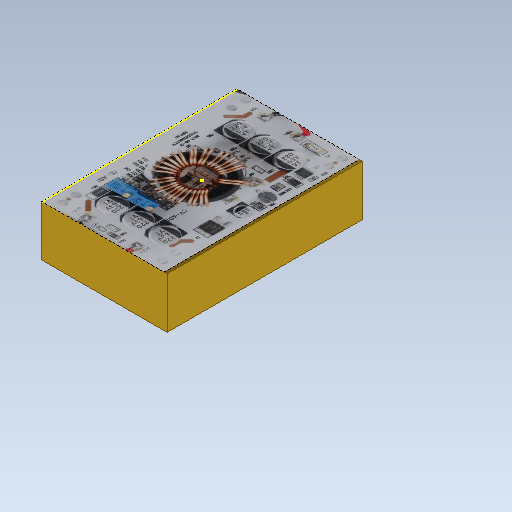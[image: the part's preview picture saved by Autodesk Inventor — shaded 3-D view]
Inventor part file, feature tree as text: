
AUTODESK INVENTOR PART (.ipt)
format: ipt  version: 2020 (Build 240168000, 168)  size: 350,720 bytes
history: native  units: mm
features: other x2, sketch x2, extrude x1
ambient origin geometry x8: Origin, YZ Plane, XZ Plane, XY Plane, X Axis, Y Axis, Z Axis, Center Point
bodies: Body1 (feature_tree)
feature tree (5):
  other  "Твердое тело1"
  extrude  "Выдавливание1"  Depth=52.0mm
  sketch  "Эскиз2"
  sketch  "Эскиз1"
  other  "Картинка1"
